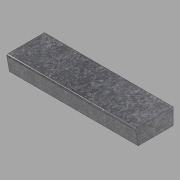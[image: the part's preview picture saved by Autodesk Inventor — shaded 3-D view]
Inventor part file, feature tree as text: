
AUTODESK INVENTOR PART (.ipt)
format: ipt  version: 2022.1 (Build 261234020, 234B)  size: 101,376 bytes
history: native  units: in
note: dims shown in document units (in); Inventor stores cm internally (conversion verified against a paired STEP export)
features: other x3, extrude x1, sketch x1
ambient origin geometry x8: Origin, YZ Plane, XZ Plane, XY Plane, X Axis, Y Axis, Z Axis, Center Point
bodies: Solid1 (feature_tree)
feature tree (5):
  other  "Blocks"
  extrude  "Extrusion1"  Depth=47.75in TaperAngle=0.0deg
  sketch  "Sketch1"  dims[d0=13.0in d1=6.0in d2=13.5in d3=0.5in d4=0.5in d5=47.75in d6=0.0in]
  other  "Profile"
  other  "Profile:1"
